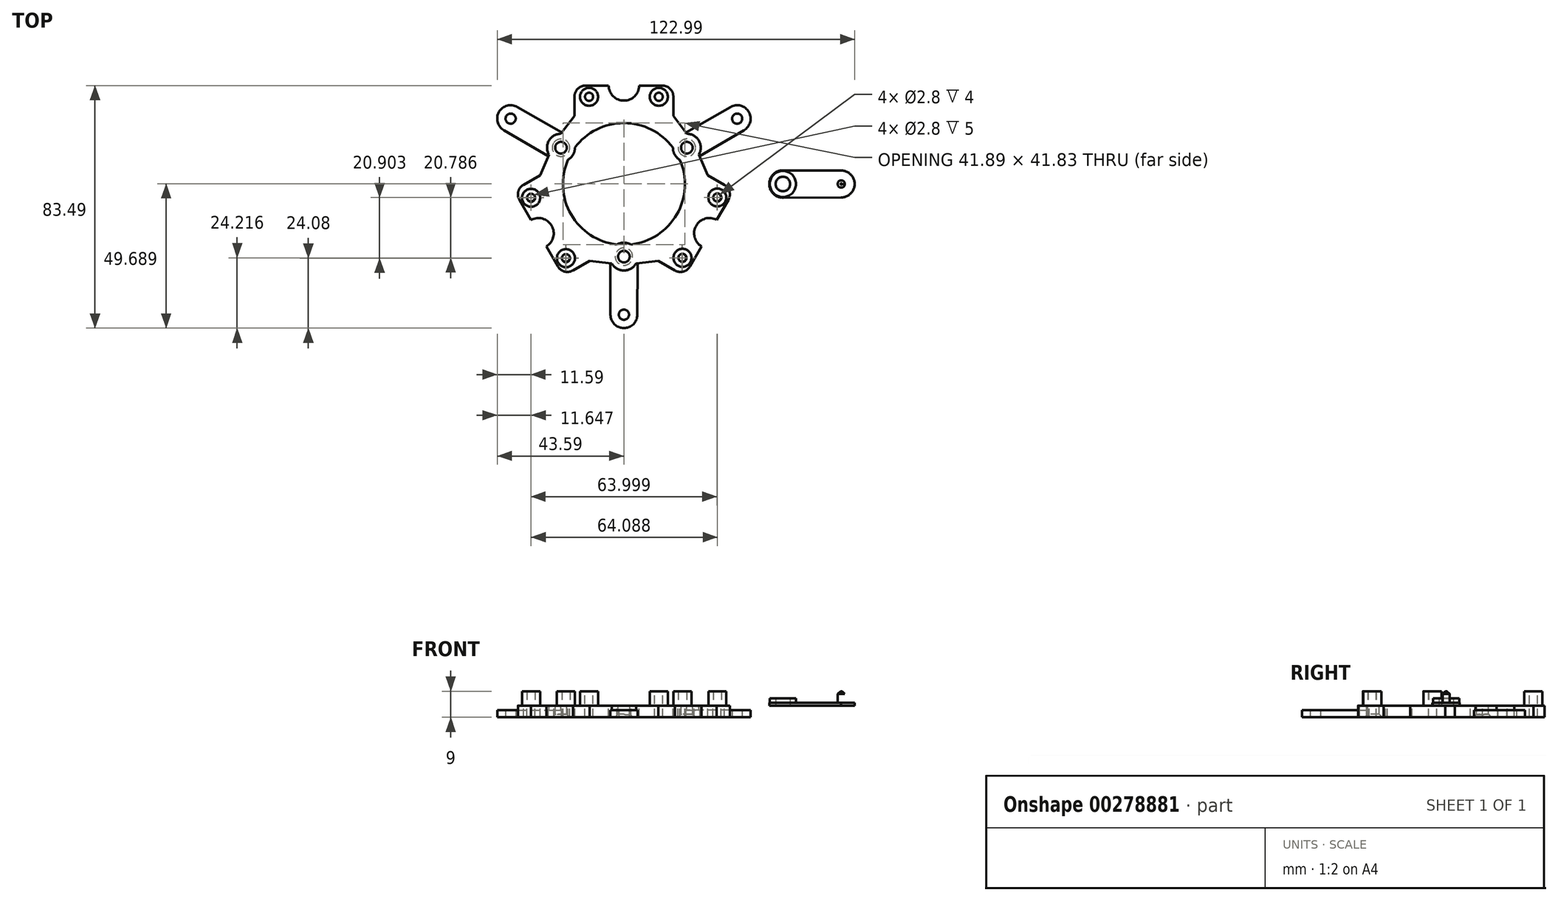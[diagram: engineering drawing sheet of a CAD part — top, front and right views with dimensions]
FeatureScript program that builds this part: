
annotation { "Feature Type Name" : "Feature", "Feature Type Description" : "" }
export const myFeature = defineFeature(function(context is Context, id is Id, definition is map)
    precondition{}
    {
        {
            var Q0;
            Q0=qCreatedBy(makeId("Front.planeOp"),FACE);
            var sketch = newSketch(context, id + "F0", { "sketchPlane" : qUnion([Q0])});
            skLineSegment(sketch, "E0", {"start": v(0, 0) * mm, "end": v(0, 50) * mm});
            skSolve(sketch);
        }
        {
            var Q0;
            Q0=qCreatedBy(makeId("Top.planeOp"),FACE);
            var sketch = newSketch(context, id + "F1", { "sketchPlane" : qUnion([Q0])});
            skCircle(sketch, "E1.cCircle", {"center": v(0, 0) * mm, "radius": 30.02 * mm, "construction": true});
            skLineSegment(sketch, "E1.0", {"start": v(-52, 30.02) * mm, "end": v(52, 30.02) * mm});
            skLineSegment(sketch, "E1.1", {"start": v(52, 30.02) * mm, "end": v(0, -60.04) * mm});
            skLineSegment(sketch, "E1.2", {"start": v(0, -60.04) * mm, "end": v(-52, 30.02) * mm});
            skPoint(sketch, "E1.0.midPoint", {"position": v(0, 30.02) * mm});
            skCircle(sketch, "E2", {"center": v(12, 30.02) * mm, "radius": 1.25 * mm});
            skCircle(sketch, "E3.MirrorC", {"center": v(-12, 30.02) * mm, "radius": 1.25 * mm});
            skCircle(sketch, "E4.1.0", {"center": v(-32, -4.62) * mm, "radius": 1.25 * mm});
            skCircle(sketch, "E4.1.1", {"center": v(-20, -25.4) * mm, "radius": 1.25 * mm});
            skCircle(sketch, "E4.2.0", {"center": v(20, -25.4) * mm, "radius": 1.25 * mm});
            skCircle(sketch, "E4.2.1", {"center": v(32, -4.62) * mm, "radius": 1.25 * mm});
            skSolve(sketch);
        }
        {
            var Q0;
            Q0=qCreatedBy(makeId("Top.planeOp"),FACE);
            var sketch = newSketch(context, id + "F2", { "sketchPlane" : qUnion([Q0])});
            skLineSegment(sketch, "E5", {"start": v(5.25, 33.87) * mm, "end": v(10.75, 33.87) * mm});
            skArc(sketch, "E6", {"start": v(16.85, 12.5) * mm, "mid": v(9.43, 18.74) * mm, "end": v(0, 20.98) * mm});
            skArc(sketch, "E7", {"start": v(0, 28.71) * mm, "mid": v(3.68, 30.22) * mm, "end": v(5.25, 33.87) * mm});
            skLineSegment(sketch, "E8", {"start": v(10.75, 33.87) * mm, "end": v(13.25, 33.87) * mm});
            skLineSegment(sketch, "E9", {"start": v(12, 33.87) * mm, "end": v(12, 30.02) * mm});
            skCircle(sketch, "E10", {"center": v(21.65, 12.5) * mm, "radius": 2 * mm});
            skArc(sketch, "E11", {"start": v(16.85, 12.5) * mm, "mid": v(25.04, 9.1) * mm, "end": v(21.65, 17.3) * mm});
            skArc(sketch, "E12", {"start": v(17, 30.02) * mm, "mid": v(15.94, 32.74) * mm, "end": v(13.25, 33.87) * mm});
            skLineSegment(sketch, "E13", {"start": v(17, 30.02) * mm, "end": v(17, 23.47) * mm});
            skLineSegment(sketch, "E14", {"start": v(17, 23.47) * mm, "end": v(21.65, 17.3) * mm});
            skLineSegment(sketch, "E15.MirrorCS", {"start": v(-10.75, 33.87) * mm, "end": v(-13.25, 33.87) * mm});
            skLineSegment(sketch, "E16.MirrorCS", {"start": v(-12, 33.87) * mm, "end": v(-12, 30.02) * mm});
            skLineSegment(sketch, "E17.MirrorCS", {"start": v(-17, 23.47) * mm, "end": v(-21.65, 17.3) * mm});
            skArc(sketch, "E18.MirrorCS", {"start": v(-16.85, 12.5) * mm, "mid": v(-25.04, 9.1) * mm, "end": v(-21.65, 17.3) * mm});
            skLineSegment(sketch, "E19.MirrorCS", {"start": v(-5.25, 33.87) * mm, "end": v(-10.75, 33.87) * mm});
            skLineSegment(sketch, "E20.MirrorCS", {"start": v(-17, 30.02) * mm, "end": v(-17, 23.47) * mm});
            skArc(sketch, "E21.MirrorCS", {"start": v(-17, 30.02) * mm, "mid": v(-15.94, 32.74) * mm, "end": v(-13.25, 33.87) * mm});
            skCircle(sketch, "E22.MirrorC", {"center": v(-21.65, 12.5) * mm, "radius": 2 * mm});
            skArc(sketch, "E23.MirrorCS", {"start": v(0, 28.71) * mm, "mid": v(-3.68, 30.22) * mm, "end": v(-5.25, 33.87) * mm});
            skArc(sketch, "E24.MirrorCS", {"start": v(-16.85, 12.5) * mm, "mid": v(-9.43, 18.74) * mm, "end": v(0, 20.98) * mm});
            skArc(sketch, "E25.1.0", {"start": v(-24.87, -14.36) * mm, "mid": v(-28, -11.92) * mm, "end": v(-31.96, -12.39) * mm});
            skLineSegment(sketch, "E25.1.1", {"start": v(-23.33, -27.33) * mm, "end": v(-20, -25.4) * mm});
            skArc(sketch, "E25.1.2", {"start": v(-19.25, 8.34) * mm, "mid": v(-20.4, 17.14) * mm, "end": v(-25.8, 10.1) * mm});
            skLineSegment(sketch, "E25.1.4", {"start": v(-31.96, -12.39) * mm, "end": v(-34.7, -7.63) * mm});
            skLineSegment(sketch, "E25.1.5", {"start": v(-35.33, -6.54) * mm, "end": v(-32, -4.62) * mm});
            skArc(sketch, "E25.1.6", {"start": v(-19.25, 8.34) * mm, "mid": v(-20.95, -1.2) * mm, "end": v(-18.17, -10.5) * mm});
            skArc(sketch, "E25.1.7", {"start": v(-34.5, -0.29) * mm, "mid": v(-36.32, -2.57) * mm, "end": v(-35.96, -5.46) * mm});
            skArc(sketch, "E25.1.8", {"start": v(-24.87, -14.36) * mm, "mid": v(-24.33, -18.3) * mm, "end": v(-26.7, -21.48) * mm});
            skCircle(sketch, "E25.1.9", {"center": v(0, -25) * mm, "radius": 2 * mm});
            skLineSegment(sketch, "E25.1.10", {"start": v(-28.83, 2.99) * mm, "end": v(-25.8, 10.1) * mm});
            skArc(sketch, "E25.1.11", {"start": v(-2.4, -20.84) * mm, "mid": v(-11.51, -17.54) * mm, "end": v(-18.17, -10.5) * mm});
            skArc(sketch, "E25.1.12", {"start": v(-17.5, -29.73) * mm, "mid": v(-20.38, -30.17) * mm, "end": v(-22.7, -28.41) * mm});
            skLineSegment(sketch, "E25.1.13", {"start": v(-34.5, -0.29) * mm, "end": v(-28.83, 2.99) * mm});
            skArc(sketch, "E25.1.14", {"start": v(-2.4, -20.84) * mm, "mid": v(4.64, -26.24) * mm, "end": v(-4.16, -27.4) * mm});
            skLineSegment(sketch, "E25.1.15", {"start": v(-26.7, -21.48) * mm, "end": v(-23.96, -26.24) * mm});
            skLineSegment(sketch, "E25.1.16", {"start": v(-11.83, -26.46) * mm, "end": v(-4.16, -27.4) * mm});
            skLineSegment(sketch, "E25.1.17", {"start": v(-17.5, -29.73) * mm, "end": v(-11.83, -26.46) * mm});
            skLineSegment(sketch, "E25.1.18", {"start": v(-34.7, -7.63) * mm, "end": v(-35.96, -5.46) * mm});
            skLineSegment(sketch, "E25.1.19", {"start": v(-23.96, -26.24) * mm, "end": v(-22.7, -28.41) * mm});
            skArc(sketch, "E25.2.0", {"start": v(24.87, -14.36) * mm, "mid": v(24.33, -18.3) * mm, "end": v(26.7, -21.48) * mm});
            skLineSegment(sketch, "E25.2.1", {"start": v(35.33, -6.54) * mm, "end": v(32, -4.62) * mm});
            skArc(sketch, "E25.2.2", {"start": v(2.4, -20.84) * mm, "mid": v(-4.64, -26.24) * mm, "end": v(4.16, -27.4) * mm});
            skCircle(sketch, "E25.2.3", {"center": v(0, -25) * mm, "radius": 2 * mm});
            skLineSegment(sketch, "E25.2.4", {"start": v(26.7, -21.48) * mm, "end": v(23.96, -26.24) * mm});
            skLineSegment(sketch, "E25.2.5", {"start": v(23.33, -27.33) * mm, "end": v(20, -25.4) * mm});
            skArc(sketch, "E25.2.6", {"start": v(2.4, -20.84) * mm, "mid": v(11.51, -17.54) * mm, "end": v(18.17, -10.5) * mm});
            skArc(sketch, "E25.2.7", {"start": v(17.5, -29.73) * mm, "mid": v(20.38, -30.17) * mm, "end": v(22.7, -28.41) * mm});
            skArc(sketch, "E25.2.8", {"start": v(24.87, -14.36) * mm, "mid": v(28, -11.92) * mm, "end": v(31.96, -12.39) * mm});
            skLineSegment(sketch, "E25.2.10", {"start": v(11.83, -26.46) * mm, "end": v(4.16, -27.4) * mm});
            skArc(sketch, "E25.2.11", {"start": v(19.25, 8.34) * mm, "mid": v(20.95, -1.2) * mm, "end": v(18.17, -10.5) * mm});
            skArc(sketch, "E25.2.12", {"start": v(34.5, -0.29) * mm, "mid": v(36.32, -2.57) * mm, "end": v(35.96, -5.46) * mm});
            skLineSegment(sketch, "E25.2.13", {"start": v(17.5, -29.73) * mm, "end": v(11.83, -26.46) * mm});
            skArc(sketch, "E25.2.14", {"start": v(19.25, 8.34) * mm, "mid": v(20.4, 17.14) * mm, "end": v(25.8, 10.1) * mm});
            skLineSegment(sketch, "E25.2.15", {"start": v(31.96, -12.39) * mm, "end": v(34.7, -7.63) * mm});
            skLineSegment(sketch, "E25.2.16", {"start": v(28.83, 2.99) * mm, "end": v(25.8, 10.1) * mm});
            skLineSegment(sketch, "E25.2.17", {"start": v(34.5, -0.29) * mm, "end": v(28.83, 2.99) * mm});
            skLineSegment(sketch, "E25.2.18", {"start": v(23.96, -26.24) * mm, "end": v(22.7, -28.41) * mm});
            skLineSegment(sketch, "E25.2.19", {"start": v(34.7, -7.63) * mm, "end": v(35.96, -5.46) * mm});
            skCircle(sketch, "E26", {"center": v(12, 30.02) * mm, "radius": 1.4 * mm});
            skCircle(sketch, "E27.MirrorC", {"center": v(-12, 30.02) * mm, "radius": 1.4 * mm});
            skCircle(sketch, "E28.1.0", {"center": v(-32, -4.62) * mm, "radius": 1.4 * mm});
            skCircle(sketch, "E28.1.1", {"center": v(-20, -25.4) * mm, "radius": 1.4 * mm});
            skCircle(sketch, "E28.2.0", {"center": v(20, -25.4) * mm, "radius": 1.4 * mm});
            skCircle(sketch, "E28.2.1", {"center": v(32, -4.62) * mm, "radius": 1.4 * mm});
            skSolve(sketch);
        }
        {
            var Q0;
            Q0=qSketchRegion(id+"F2",true);
            extrude(context, id + "F3", {"entities" : qUnion([Q0]), "oppositeDirection" : true, "depth" : 4 * mm});
        }
        {
            var Q0;
            Q0=makeQuery(id+"F3.opExtrude","CAP_FACE",FACE,{"disambiguationData":[OSD([sQuery(id+"F2.wireOp",EDGE,"E5"),sQuery(id+"F2.wireOp",EDGE,"E6"),sQuery(id+"F2.wireOp",EDGE,"OTH0FymN-yfsN-0UsN-41Kz-5CJosObtJ083"),sQuery(id+"F2.wireOp",EDGE,"3A02pTdK-AV8J-qCXS-i5Cg-76qnhJVGPjWh"),sQuery(id+"F2.wireOp",EDGE,"5Z3o6wOb-oYhe-xRQF-fwUz-g2kkQ9HctwZJ"),sQuery(id+"F2.wireOp",EDGE,"E7"),sQuery(id+"F2.wireOp",EDGE,"AUobkKVc-RQ03-aKL8-U0OO-zYTzcYtjvFHw"),sQuery(id+"F2.wireOp",EDGE,"E8"),sQuery(id+"F2.wireOp",EDGE,"624812f1-2ad6-4ab7-8a89-68286fdeb31e8.MirrorCS"),sQuery(id+"F2.wireOp",EDGE,"624812f1-2ad6-4ab7-8a89-68286fdeb31e9.MirrorCS"),sQuery(id+"F2.wireOp",EDGE,"624812f1-2ad6-4ab7-8a89-68286fdeb31e10.MirrorCS"),sQuery(id+"F2.wireOp",EDGE,"624812f1-2ad6-4ab7-8a89-68286fdeb31e11.MirrorCS"),sQuery(id+"F2.wireOp",EDGE,"624812f1-2ad6-4ab7-8a89-68286fdeb31e12.MirrorCS"),sQuery(id+"F2.wireOp",EDGE,"624812f1-2ad6-4ab7-8a89-68286fdeb31e14.MirrorCS"),sQuery(id+"F2.wireOp",EDGE,"624812f1-2ad6-4ab7-8a89-68286fdeb31e15.MirrorCS"),sQuery(id+"F2.wireOp",EDGE,"624812f1-2ad6-4ab7-8a89-68286fdeb31e16.MirrorCS"),sQuery(id+"F2.wireOp",EDGE,"36ff6b61-fbfb-4fdb-958a-ac3ee2e7cda7.1.1"),sQuery(id+"F2.wireOp",EDGE,"36ff6b61-fbfb-4fdb-958a-ac3ee2e7cda7.1.2"),sQuery(id+"F2.wireOp",EDGE,"36ff6b61-fbfb-4fdb-958a-ac3ee2e7cda7.1.3"),sQuery(id+"F2.wireOp",EDGE,"36ff6b61-fbfb-4fdb-958a-ac3ee2e7cda7.1.4"),sQuery(id+"F2.wireOp",EDGE,"36ff6b61-fbfb-4fdb-958a-ac3ee2e7cda7.1.5"),sQuery(id+"F2.wireOp",EDGE,"36ff6b61-fbfb-4fdb-958a-ac3ee2e7cda7.1.6"),sQuery(id+"F2.wireOp",EDGE,"36ff6b61-fbfb-4fdb-958a-ac3ee2e7cda7.1.7"),sQuery(id+"F2.wireOp",EDGE,"36ff6b61-fbfb-4fdb-958a-ac3ee2e7cda7.1.8"),sQuery(id+"F2.wireOp",EDGE,"36ff6b61-fbfb-4fdb-958a-ac3ee2e7cda7.1.9"),sQuery(id+"F2.wireOp",EDGE,"36ff6b61-fbfb-4fdb-958a-ac3ee2e7cda7.1.10"),sQuery(id+"F2.wireOp",EDGE,"36ff6b61-fbfb-4fdb-958a-ac3ee2e7cda7.1.11"),sQuery(id+"F2.wireOp",EDGE,"36ff6b61-fbfb-4fdb-958a-ac3ee2e7cda7.1.12"),sQuery(id+"F2.wireOp",EDGE,"36ff6b61-fbfb-4fdb-958a-ac3ee2e7cda7.1.15"),sQuery(id+"F2.wireOp",EDGE,"36ff6b61-fbfb-4fdb-958a-ac3ee2e7cda7.1.16"),sQuery(id+"F2.wireOp",EDGE,"36ff6b61-fbfb-4fdb-958a-ac3ee2e7cda7.1.17"),sQuery(id+"F2.wireOp",EDGE,"36ff6b61-fbfb-4fdb-958a-ac3ee2e7cda7.1.19"),sQuery(id+"F2.wireOp",EDGE,"36ff6b61-fbfb-4fdb-958a-ac3ee2e7cda7.2.1"),sQuery(id+"F2.wireOp",EDGE,"36ff6b61-fbfb-4fdb-958a-ac3ee2e7cda7.2.2"),sQuery(id+"F2.wireOp",EDGE,"36ff6b61-fbfb-4fdb-958a-ac3ee2e7cda7.2.3"),sQuery(id+"F2.wireOp",EDGE,"36ff6b61-fbfb-4fdb-958a-ac3ee2e7cda7.2.4"),sQuery(id+"F2.wireOp",EDGE,"36ff6b61-fbfb-4fdb-958a-ac3ee2e7cda7.2.5"),sQuery(id+"F2.wireOp",EDGE,"36ff6b61-fbfb-4fdb-958a-ac3ee2e7cda7.2.6"),sQuery(id+"F2.wireOp",EDGE,"36ff6b61-fbfb-4fdb-958a-ac3ee2e7cda7.2.7"),sQuery(id+"F2.wireOp",EDGE,"36ff6b61-fbfb-4fdb-958a-ac3ee2e7cda7.2.8"),sQuery(id+"F2.wireOp",EDGE,"36ff6b61-fbfb-4fdb-958a-ac3ee2e7cda7.2.9"),sQuery(id+"F2.wireOp",EDGE,"36ff6b61-fbfb-4fdb-958a-ac3ee2e7cda7.2.10"),sQuery(id+"F2.wireOp",EDGE,"36ff6b61-fbfb-4fdb-958a-ac3ee2e7cda7.2.11"),sQuery(id+"F2.wireOp",EDGE,"36ff6b61-fbfb-4fdb-958a-ac3ee2e7cda7.2.12"),sQuery(id+"F2.wireOp",EDGE,"36ff6b61-fbfb-4fdb-958a-ac3ee2e7cda7.2.15"),sQuery(id+"F2.wireOp",EDGE,"36ff6b61-fbfb-4fdb-958a-ac3ee2e7cda7.2.16"),sQuery(id+"F2.wireOp",EDGE,"36ff6b61-fbfb-4fdb-958a-ac3ee2e7cda7.2.17"),sQuery(id+"F2.wireOp",EDGE,"36ff6b61-fbfb-4fdb-958a-ac3ee2e7cda7.2.19")])],"isStart":true});
            var sketch = newSketch(context, id + "F4", { "sketchPlane" : qUnion([Q0])});
            skCircle(sketch, "E29", {"center": v(12, 30.02) * mm, "radius": 1.4 * mm});
            skCircle(sketch, "E30", {"center": v(12, 30.02) * mm, "radius": 3.1 * mm});
            skCircle(sketch, "E31.MirrorC", {"center": v(-12, 30.02) * mm, "radius": 1.4 * mm});
            skCircle(sketch, "E32.MirrorC", {"center": v(-12, 30.02) * mm, "radius": 3.1 * mm});
            skCircle(sketch, "E33.1.0", {"center": v(-19.94, -25.54) * mm, "radius": 3.1 * mm});
            skCircle(sketch, "E33.1.1", {"center": v(-31.94, -4.75) * mm, "radius": 3.1 * mm});
            skCircle(sketch, "E33.1.2", {"center": v(-19.94, -25.54) * mm, "radius": 1.4 * mm});
            skCircle(sketch, "E33.1.3", {"center": v(-31.94, -4.75) * mm, "radius": 1.4 * mm});
            skCircle(sketch, "E33.2.0", {"center": v(32.15, -4.64) * mm, "radius": 3.1 * mm});
            skCircle(sketch, "E33.2.1", {"center": v(20.15, -25.42) * mm, "radius": 3.1 * mm});
            skCircle(sketch, "E33.2.2", {"center": v(32.15, -4.64) * mm, "radius": 1.4 * mm});
            skCircle(sketch, "E33.2.3", {"center": v(20.15, -25.42) * mm, "radius": 1.4 * mm});
            skPoint(sketch, "E33.center", {"position": v(0.07, -0.05) * mm});
            skSolve(sketch);
        }
        {
            var Q0;
            Q0=qSketchRegion(id+"F4",true);
            extrude(context, id + "F5", {"entities" : qUnion([Q0]), "operationType" : NewBodyOperationType.ADD, "depth" : 5 * mm});
        }
        {
            var Q0;
            Q0=qCreatedBy(makeId("Top.planeOp"),FACE);
            cPlane(context, id + "F6", {"entities" : qUnion([Q0]), "cplaneType" : CPlaneType.OFFSET, "offset" : 2 * mm, "oppositeDirection" : true, "width" : 150 * mm, "height" : 150 * mm});
        }
        {
            var Q0;
            Q0=makeQuery(id+"F3.opExtrude","CAP_FACE",FACE,{"disambiguationData":[OSD([sQuery(id+"F2.wireOp",EDGE,"E5"),sQuery(id+"F2.wireOp",EDGE,"E6"),sQuery(id+"F2.wireOp",EDGE,"E7"),sQuery(id+"F2.wireOp",EDGE,"E8"),sQuery(id+"F2.wireOp",EDGE,"E10"),sQuery(id+"F2.wireOp",EDGE,"E11"),sQuery(id+"F2.wireOp",EDGE,"E12"),sQuery(id+"F2.wireOp",EDGE,"E13"),sQuery(id+"F2.wireOp",EDGE,"E14"),sQuery(id+"F2.wireOp",EDGE,"E15.MirrorCS"),sQuery(id+"F2.wireOp",EDGE,"E17.MirrorCS"),sQuery(id+"F2.wireOp",EDGE,"E18.MirrorCS"),sQuery(id+"F2.wireOp",EDGE,"E19.MirrorCS"),sQuery(id+"F2.wireOp",EDGE,"E20.MirrorCS"),sQuery(id+"F2.wireOp",EDGE,"E21.MirrorCS"),sQuery(id+"F2.wireOp",EDGE,"E22.MirrorC"),sQuery(id+"F2.wireOp",EDGE,"E23.MirrorCS"),sQuery(id+"F2.wireOp",EDGE,"E24.MirrorCS"),sQuery(id+"F2.wireOp",EDGE,"E25.1.0"),sQuery(id+"F2.wireOp",EDGE,"E25.1.2"),sQuery(id+"F2.wireOp",EDGE,"E22.MirrorC"),sQuery(id+"F2.wireOp",EDGE,"E25.1.4"),sQuery(id+"F2.wireOp",EDGE,"E25.1.6"),sQuery(id+"F2.wireOp",EDGE,"E25.1.7"),sQuery(id+"F2.wireOp",EDGE,"E25.1.8"),sQuery(id+"F2.wireOp",EDGE,"E25.1.9"),sQuery(id+"F2.wireOp",EDGE,"E25.1.10"),sQuery(id+"F2.wireOp",EDGE,"E25.1.11"),sQuery(id+"F2.wireOp",EDGE,"E25.1.12"),sQuery(id+"F2.wireOp",EDGE,"E25.1.13"),sQuery(id+"F2.wireOp",EDGE,"E25.1.14"),sQuery(id+"F2.wireOp",EDGE,"E25.1.15"),sQuery(id+"F2.wireOp",EDGE,"E25.1.16"),sQuery(id+"F2.wireOp",EDGE,"E25.1.17"),sQuery(id+"F2.wireOp",EDGE,"E25.1.18"),sQuery(id+"F2.wireOp",EDGE,"E25.1.19"),sQuery(id+"F2.wireOp",EDGE,"E25.2.0"),sQuery(id+"F2.wireOp",EDGE,"E25.2.2"),sQuery(id+"F2.wireOp",EDGE,"E25.2.3"),sQuery(id+"F2.wireOp",EDGE,"E25.2.4"),sQuery(id+"F2.wireOp",EDGE,"E25.2.6"),sQuery(id+"F2.wireOp",EDGE,"E25.2.7"),sQuery(id+"F2.wireOp",EDGE,"E25.2.8"),sQuery(id+"F2.wireOp",EDGE,"E10"),sQuery(id+"F2.wireOp",EDGE,"E25.2.10"),sQuery(id+"F2.wireOp",EDGE,"E25.2.11"),sQuery(id+"F2.wireOp",EDGE,"E25.2.12"),sQuery(id+"F2.wireOp",EDGE,"E25.2.13"),sQuery(id+"F2.wireOp",EDGE,"E25.2.14"),sQuery(id+"F2.wireOp",EDGE,"E25.2.15"),sQuery(id+"F2.wireOp",EDGE,"E25.2.16"),sQuery(id+"F2.wireOp",EDGE,"E25.2.17"),sQuery(id+"F2.wireOp",EDGE,"E25.2.18"),sQuery(id+"F2.wireOp",EDGE,"E25.2.19")])],"isStart":false});
            var sketch = newSketch(context, id + "F7", { "sketchPlane" : qUnion([Q0])});
            skLineSegment(sketch, "E34", {"start": v(0, 0) * mm, "end": v(21.65, -12.5) * mm});
            skCircle(sketch, "E35", {"center": v(21.65, -12.5) * mm, "radius": 4.7 * mm});
            skLineSegment(sketch, "E36", {"start": v(21.65, -12.5) * mm, "end": v(19.3, -16.57) * mm});
            skLineSegment(sketch, "E37", {"start": v(21.65, -12.5) * mm, "end": v(37.45, -21.62) * mm});
            skArc(sketch, "E38", {"start": v(37.45, -21.62) * mm, "mid": v(38.1, -24.01) * mm, "end": v(40.49, -23.37) * mm});
            skArc(sketch, "E39", {"start": v(36.66, -26.5) * mm, "mid": v(40.17, -26.96) * mm, "end": v(42.98, -24.8) * mm});
            skLineSegment(sketch, "E40", {"start": v(40.49, -23.37) * mm, "end": v(42.98, -24.8) * mm});
            skArc(sketch, "E41.MirrorCS", {"start": v(37.45, -21.62) * mm, "mid": v(39.84, -20.98) * mm, "end": v(40.49, -23.37) * mm});
            skCircle(sketch, "E42", {"center": v(21.65, -12.5) * mm, "radius": 2.5 * mm});
            skLineSegment(sketch, "E43", {"start": v(36.66, -26.5) * mm, "end": v(19.3, -16.57) * mm});
            skLineSegment(sketch, "E44.MirrorCS", {"start": v(41.29, -18.5) * mm, "end": v(24, -8.43) * mm});
            skArc(sketch, "E45.MirrorCS", {"start": v(41.29, -18.5) * mm, "mid": v(43.44, -21.3) * mm, "end": v(42.98, -24.8) * mm});
            skSolve(sketch);
        }
        {
            var Q0;
            Q0=qSketchRegion(id+"F7",true);
            extrude(context, id + "F8", {"entities" : qUnion([Q0]), "oppositeDirection" : true, "depth" : 2.5 * mm});
        }
        {
            var Q0;
            Q0=makeQuery(id+"F8.opExtrude","SWEPT_BODY",BODY,{"disambiguationData":[OSD([sQuery(id+"F7.wireOp",EDGE,"E35"),sQuery(id+"F7.wireOp",EDGE,"E38"),sQuery(id+"F7.wireOp",EDGE,"E39"),sQuery(id+"F7.wireOp",EDGE,"9kqUA9Jo-edwP-NO00-sSji-nR2odCKgbMeb"),sQuery(id+"F7.wireOp",EDGE,"GDexJB8U-NTdd-inDH-WQeI-0l2QnxEohQ9h"),sQuery(id+"F7.wireOp",EDGE,"JeVKlujZ-zA6a-IIGW-YSz6-gVSeSdLv3vhB"),sQuery(id+"F7.wireOp",EDGE,"MW1JaytO-XEjq-5YeB-MR8k-oZC2Z9Jpgj3d"),sQuery(id+"F7.wireOp",EDGE,"Y6P3fMeu-8VPu-QNSC-VJmo-vZOKqAch7LHx"),sQuery(id+"F7.wireOp",EDGE,"4fPfChJr-W4YN-7BBy-D4l4-nojVqKYKC0ln"),sQuery(id+"F7.wireOp",EDGE,"2de3917a-e362-44b2-9ee0-3e3d1b5f62ab.trimOffspring"),sQuery(id+"F7.wireOp",EDGE,"E40"),sQuery(id+"F7.wireOp",EDGE,"7557a1f4-8a86-41d2-b121-450dcfc2fc1b0.MirrorCS"),sQuery(id+"F7.wireOp",EDGE,"d8fe862a-e72c-42c7-bef4-22f0e19987d60.MirrorCS"),sQuery(id+"F7.wireOp",EDGE,"e1d4639a-9bbe-4f0b-9f0e-1e47ea0f83f50.MirrorCS"),sQuery(id+"F7.wireOp",EDGE,"bf0646c6-655b-4980-9d40-1a8a652c793b0.MirrorCS"),sQuery(id+"F7.wireOp",EDGE,"28871922-5b9a-4380-b66f-36384049dd340.MirrorCS"),sQuery(id+"F7.wireOp",EDGE,"f77bd1d0-2b69-4607-9877-85ea826859d50.MirrorCS"),sQuery(id+"F7.wireOp",EDGE,"4006c2c9-1f6f-453f-8150-a3eb66e0c37a0.MirrorCS"),sQuery(id+"F7.wireOp",EDGE,"1c3aa9cd-c4e5-4692-9f40-bda29d6e96f20.MirrorCS"),sQuery(id+"F7.wireOp",EDGE,"E40"),sQuery(id+"F7.wireOp",EDGE,"E41.MirrorCS"),sQuery(id+"F7.wireOp",EDGE,"E42")])]});
            var Q1;
            Q1=sQuery(id+"F0.wireOp",EDGE,"E0");
            circularPattern(context, id + "F9", {"operationType" : NewBodyOperationType.ADD, "entities" : qUnion([Q0]), "axis" : qUnion([Q1]), "angle" : 360 * degree, "instanceCount" : 3, "equalSpace" : true});
        }
        {
            var Q0;
            Q0=makeQuery(id+"F3.opExtrude","CAP_EDGE",EDGE,{"disambiguationData":[OSD([sQuery(id+"F2.wireOp",EDGE,"E22.MirrorC")])],"isStart":false});
            var Q1;
            Q1=makeQuery(id+"F3.opExtrude","CAP_EDGE",EDGE,{"disambiguationData":[OSD([sQuery(id+"F2.wireOp",EDGE,"E10")])],"isStart":false});
            var Q2;
            Q2=makeQuery(id+"F3.opExtrude","CAP_EDGE",EDGE,{"disambiguationData":[OSD([sQuery(id+"F2.wireOp",EDGE,"E25.1.9")])],"isStart":false});
            chamfer(context, id + "F10", {"entities" : qUnion([Q0, Q1, Q2]), "width" : 1 * mm, "tangentPropagation" : true});
        }
        {
            var Q0;
            Q0=qCreatedBy(makeId("Top.planeOp"),FACE);
            var sketch = newSketch(context, id + "F11", { "sketchPlane" : qUnion([Q0])});
            skCircle(sketch, "E46", {"center": v(54.7, 0) * mm, "radius": 4.7 * mm});
            skLineSegment(sketch, "E47", {"start": v(54.7, 0) * mm, "end": v(54.7, -4.7) * mm});
            skLineSegment(sketch, "E48", {"start": v(54.7, 0) * mm, "end": v(73.53, 0) * mm});
            skArc(sketch, "E49", {"start": v(73.53, 0) * mm, "mid": v(74.78, -1.25) * mm, "end": v(76.03, 0) * mm});
            skArc(sketch, "E50", {"start": v(74.74, -4.62) * mm, "mid": v(78.04, -3.28) * mm, "end": v(79.4, 0) * mm});
            skLineSegment(sketch, "E51", {"start": v(76.03, 0) * mm, "end": v(79.4, 0) * mm});
            skArc(sketch, "E52.MirrorCS", {"start": v(73.53, 0) * mm, "mid": v(74.78, 1.25) * mm, "end": v(76.03, 0) * mm});
            skCircle(sketch, "E53", {"center": v(54.7, 0) * mm, "radius": 2.5 * mm});
            skLineSegment(sketch, "E54", {"start": v(74.74, -4.62) * mm, "end": v(54.7, -4.7) * mm});
            skLineSegment(sketch, "E55.MirrorCS", {"start": v(74.74, 4.63) * mm, "end": v(54.7, 4.7) * mm});
            skArc(sketch, "E56.MirrorCS", {"start": v(74.74, 4.63) * mm, "mid": v(78.04, 3.28) * mm, "end": v(79.4, 0) * mm});
            skSolve(sketch);
        }
        {
            var Q0;
            Q0 = qSketchRegion(id + "F11", true);
            extrude(context, id + "F12", {"entities" : qUnion([Q0]), "depth" : 1 * mm});
        }
        {
            var Q0;
            Q0=makeQuery(id+"F12.opExtrude","CAP_FACE",FACE,{"disambiguationData":[OSD([sQuery(id+"F11.wireOp",EDGE,"E46"),sQuery(id+"F11.wireOp",EDGE,"E49"),sQuery(id+"F11.wireOp",EDGE,"E50"),sQuery(id+"F11.wireOp",EDGE,"E51"),sQuery(id+"F11.wireOp",EDGE,"E51"),sQuery(id+"F11.wireOp",EDGE,"E52.MirrorCS"),sQuery(id+"F11.wireOp",EDGE,"E53"),sQuery(id+"F11.wireOp",EDGE,"E54"),sQuery(id+"F11.wireOp",EDGE,"E55.MirrorCS"),sQuery(id+"F11.wireOp",EDGE,"E56.MirrorCS")])],"isStart":true});
            var sketch = newSketch(context, id + "F13", { "sketchPlane" : qUnion([Q0])});
            skCircle(sketch, "E57", {"center": v(54.7, 0) * mm, "radius": 2.5 * mm});
            skCircle(sketch, "E58", {"center": v(54.7, 0) * mm, "radius": 4.5 * mm});
            skSolve(sketch);
        }
        {
            var Q0;
            Q0 = qSketchRegion(id + "F13", true);
            extrude(context, id + "F14", {"entities" : qUnion([Q0]), "operationType" : NewBodyOperationType.ADD, "oppositeDirection" : true, "depth" : 2.5 * mm});
        }
        {
            var Q0;
            Q0=makeQuery(id+"F12.opExtrude","CAP_FACE",FACE,{"disambiguationData":[OSD([sQuery(id+"F11.wireOp",EDGE,"E46"),sQuery(id+"F11.wireOp",EDGE,"E49"),sQuery(id+"F11.wireOp",EDGE,"E50"),sQuery(id+"F11.wireOp",EDGE,"E51"),sQuery(id+"F11.wireOp",EDGE,"E51"),sQuery(id+"F11.wireOp",EDGE,"E52.MirrorCS"),sQuery(id+"F11.wireOp",EDGE,"E53"),sQuery(id+"F11.wireOp",EDGE,"E54"),sQuery(id+"F11.wireOp",EDGE,"E55.MirrorCS"),sQuery(id+"F11.wireOp",EDGE,"E56.MirrorCS")])],"isStart":true});
            var sketch = newSketch(context, id + "F15", { "sketchPlane" : qUnion([Q0])});
            skCircle(sketch, "E59", {"center": v(74.78, 0) * mm, "radius": 1.25 * mm});
            skSolve(sketch);
        }
        {
            var Q0;
            Q0 = qSketchRegion(id + "F15", true);
            extrude(context, id + "F16", {"entities" : qUnion([Q0]), "operationType" : NewBodyOperationType.ADD, "oppositeDirection" : true, "depth" : 5 * mm});
        }
        {
            var Q0;
            Q0=makeQuery(id+"F16.opExtrude","CAP_EDGE",EDGE,{"disambiguationData":[OSD([sQuery(id+"F15.wireOp",EDGE,"E59")])],"isStart":false});
            chamfer(context, id + "F17", {"entities" : qUnion([Q0]), "width" : 1 * mm, "tangentPropagation" : true});
        }
    });
